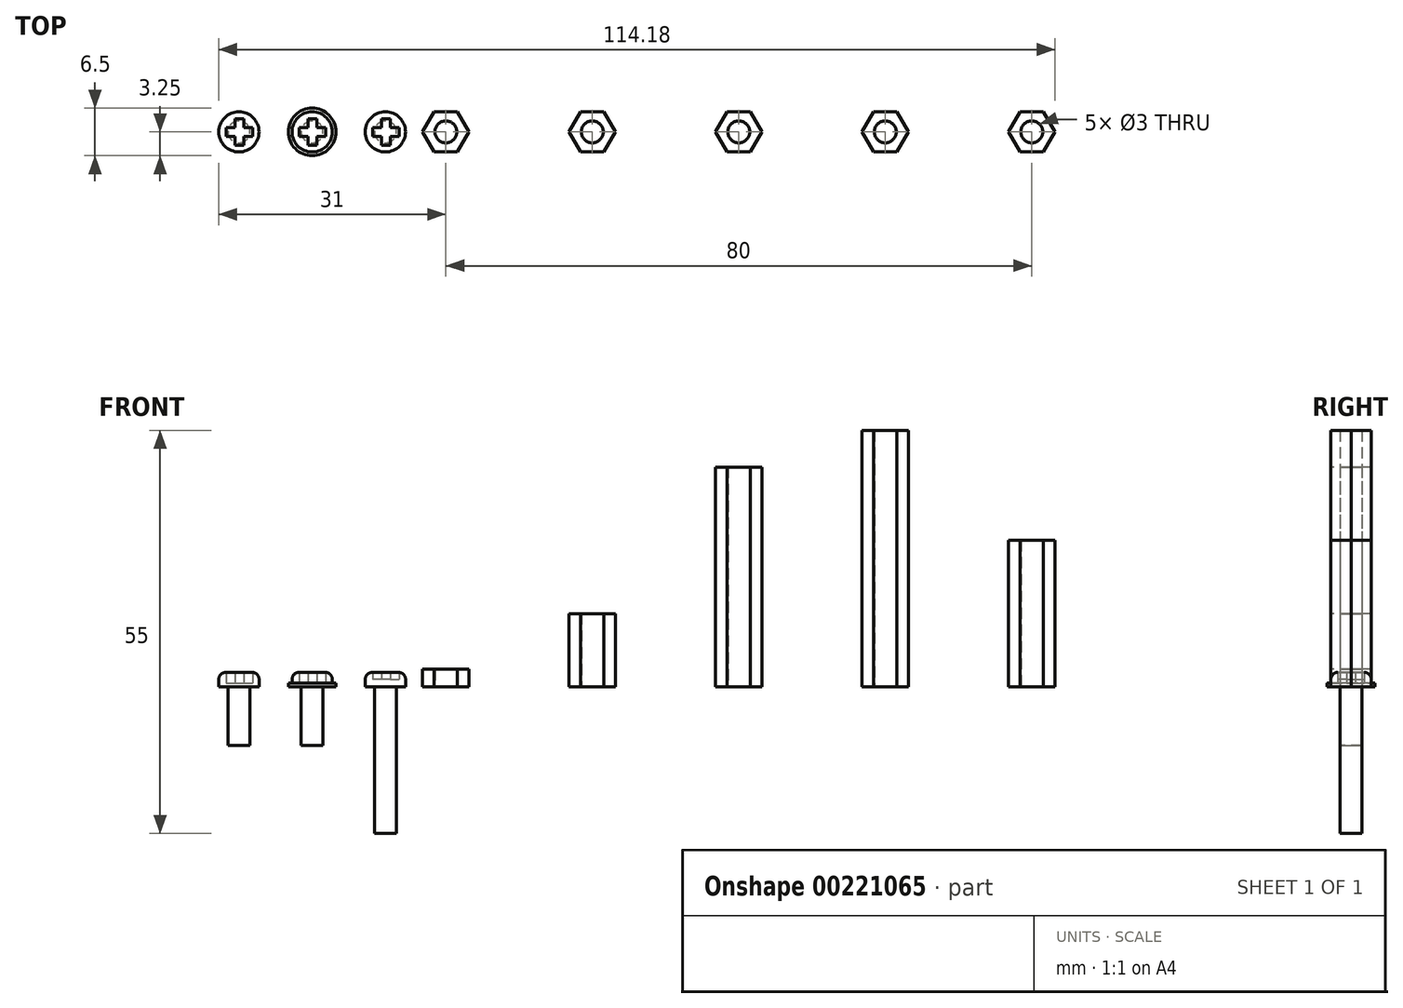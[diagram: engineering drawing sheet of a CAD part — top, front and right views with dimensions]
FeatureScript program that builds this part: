
annotation { "Feature Type Name" : "Feature", "Feature Type Description" : "" }
export const myFeature = defineFeature(function(context is Context, id is Id, definition is map)
    precondition{}
    {
        {
            var Q0;
            Q0=qCreatedBy(makeId("Top.planeOp"),FACE);
            var sketch = newSketch(context, id + "F0", { "sketchPlane" : qUnion([Q0])});
            skCircle(sketch, "E0", {"center": v(0, 0) * mm, "radius": 1.5 * mm});
            skCircle(sketch, "E1.cCircle", {"center": v(0, 0) * mm, "radius": 2.75 * mm, "construction": true});
            skLineSegment(sketch, "E1.0", {"start": v(3.18, 0) * mm, "end": v(1.59, -2.75) * mm});
            skLineSegment(sketch, "E1.1", {"start": v(1.59, -2.75) * mm, "end": v(-1.59, -2.75) * mm});
            skLineSegment(sketch, "E1.2", {"start": v(-1.59, -2.75) * mm, "end": v(-3.18, 0) * mm});
            skLineSegment(sketch, "E1.3", {"start": v(-3.18, 0) * mm, "end": v(-1.59, 2.75) * mm});
            skLineSegment(sketch, "E1.4", {"start": v(-1.59, 2.75) * mm, "end": v(1.59, 2.75) * mm});
            skLineSegment(sketch, "E1.5", {"start": v(1.59, 2.75) * mm, "end": v(3.18, 0) * mm});
            skPoint(sketch, "E1.0.midPoint", {"position": v(2.38, -1.37) * mm});
            skSolve(sketch);
        }
        {
            var Q0;
            Q0=makeQuery(id+"F0.imprint","IMPRINT",FACE,{"disambiguationData":[TD([[makeQuery(id+"F0.imprint","IMPRINT",EDGE,{"derivedFrom":sQuery(id+"F0.wireOp",EDGE,"E0")}),-1.0]])]});
            extrude(context, id + "F1", {"entities" : qUnion([Q0]), "depth" : 2.4 * mm});
        }
        {
            var Q0;
            Q0 = qSketchRegion(id + "F0", true);
            extrude(context, id + "F2", {"entities" : qUnion([Q0]), "depth" : 10 * mm});
        }
        {
            var Q0;
            Q0 = qSketchRegion(id + "F0", true);
            extrude(context, id + "F3", {"entities" : qUnion([Q0]), "depth" : 30 * mm});
        }
        {
            var Q0;
            Q0=qCreatedBy(makeId("Top.planeOp"),FACE);
            var sketch = newSketch(context, id + "F4", { "sketchPlane" : qUnion([Q0])});
            skCircle(sketch, "E2", {"center": v(-8.25, 0) * mm, "radius": 1.5 * mm});
            skCircle(sketch, "E3", {"center": v(-8.25, 0) * mm, "radius": 2.75 * mm});
            skLineSegment(sketch, "E4", {"start": v(-10, 0.6) * mm, "end": v(-10, -0.6) * mm});
            skLineSegment(sketch, "E5", {"start": v(-10, -0.6) * mm, "end": v(-8.8, -0.6) * mm});
            skLineSegment(sketch, "E6", {"start": v(-8.8, -0.6) * mm, "end": v(-8.8, -1.8) * mm});
            skLineSegment(sketch, "E7", {"start": v(-8.8, -1.8) * mm, "end": v(-7.6, -1.8) * mm});
            skLineSegment(sketch, "E8", {"start": v(-7.6, -1.8) * mm, "end": v(-7.6, -0.6) * mm});
            skLineSegment(sketch, "E9", {"start": v(-7.6, -0.6) * mm, "end": v(-6.4, -0.6) * mm});
            skLineSegment(sketch, "E10", {"start": v(-6.4, -0.6) * mm, "end": v(-6.4, 0.6) * mm});
            skLineSegment(sketch, "E11", {"start": v(-6.4, 0.6) * mm, "end": v(-7.6, 0.6) * mm});
            skLineSegment(sketch, "E12", {"start": v(-7.6, 0.6) * mm, "end": v(-7.6, 1.8) * mm});
            skLineSegment(sketch, "E13", {"start": v(-7.6, 1.8) * mm, "end": v(-8.8, 1.8) * mm});
            skLineSegment(sketch, "E14", {"start": v(-8.8, 1.8) * mm, "end": v(-8.8, 0.6) * mm});
            skLineSegment(sketch, "E15", {"start": v(-8.8, 0.6) * mm, "end": v(-10, 0.6) * mm});
            skPoint(sketch, "E16", {"position": v(-6.4, 0) * mm});
            skCircle(sketch, "E17", {"center": v(-8.25, 0) * mm, "radius": 3.25 * mm});
            skSolve(sketch);
        }
        {
            var Q0;
            Q0=makeQuery(id+"F4.imprint","IMPRINT",FACE,{"disambiguationData":[TD([[makeQuery(id+"F4.imprint","IMPRINT",EDGE,{"derivedFrom":sQuery(id+"F4.wireOp",EDGE,"E3")}),1.0]])]});
            var Q1;
            {var subQ0=sQuery(id+"F4.wireOp",EDGE,"E5");var subQ1=sQuery(id+"F4.wireOp",EDGE,"E2");var subQ2=makeQuery(id+"F4.imprint","INTERSECT",VERTEX,{"derivedFrom":[subQ1,subQ0]});Q1=makeQuery(id+"F4.imprint","IMPRINT",FACE,{"disambiguationData":[TD([[makeQuery(id+"F4.imprint","IMPRINT",EDGE,{"disambiguationData":[TD([[subQ2,-1.0]])],"derivedFrom":subQ1}),1.0]])]});}
            var Q2;
            {var subQ5=sQuery(id+"F4.wireOp",EDGE,"E4");Q2=makeQuery(id+"F4.imprint","IMPRINT",FACE,{"disambiguationData":[TD([[makeQuery(id+"F4.imprint","IMPRINT",EDGE,{"derivedFrom":subQ5}),1.0]])]});}
            var Q3;
            {var subQ5=sQuery(id+"F4.wireOp",EDGE,"E7");Q3=makeQuery(id+"F4.imprint","IMPRINT",FACE,{"disambiguationData":[TD([[makeQuery(id+"F4.imprint","IMPRINT",EDGE,{"derivedFrom":subQ5}),1.0]])]});}
            var Q4;
            {var subQ0=sQuery(id+"F4.wireOp",EDGE,"E8");var subQ1=sQuery(id+"F4.wireOp",EDGE,"E2");var subQ2=makeQuery(id+"F4.imprint","INTERSECT",VERTEX,{"derivedFrom":[subQ1,subQ0]});Q4=makeQuery(id+"F4.imprint","IMPRINT",FACE,{"disambiguationData":[TD([[makeQuery(id+"F4.imprint","IMPRINT",EDGE,{"disambiguationData":[TD([[subQ2,-1.0]])],"derivedFrom":subQ1}),1.0]])]});}
            var Q5;
            {var subQ5=sQuery(id+"F4.wireOp",EDGE,"E10");Q5=makeQuery(id+"F4.imprint","IMPRINT",FACE,{"disambiguationData":[TD([[makeQuery(id+"F4.imprint","IMPRINT",EDGE,{"derivedFrom":subQ5}),1.0]])]});}
            var Q6;
            {var subQ0=sQuery(id+"F4.wireOp",EDGE,"E12");var subQ1=sQuery(id+"F4.wireOp",EDGE,"E2");var subQ2=makeQuery(id+"F4.imprint","INTERSECT",VERTEX,{"derivedFrom":[subQ1,subQ0]});Q6=makeQuery(id+"F4.imprint","IMPRINT",FACE,{"disambiguationData":[TD([[makeQuery(id+"F4.imprint","IMPRINT",EDGE,{"disambiguationData":[TD([[subQ2,1.0]])],"derivedFrom":subQ1}),1.0]])]});}
            var Q7;
            {var subQ5=sQuery(id+"F4.wireOp",EDGE,"E13");Q7=makeQuery(id+"F4.imprint","IMPRINT",FACE,{"disambiguationData":[TD([[makeQuery(id+"F4.imprint","IMPRINT",EDGE,{"derivedFrom":subQ5}),1.0]])]});}
            var Q8;
            {var subQ0=sQuery(id+"F4.wireOp",EDGE,"E14");var subQ1=sQuery(id+"F4.wireOp",EDGE,"E2");var subQ2=makeQuery(id+"F4.imprint","INTERSECT",VERTEX,{"derivedFrom":[subQ1,subQ0]});Q8=makeQuery(id+"F4.imprint","IMPRINT",FACE,{"disambiguationData":[TD([[makeQuery(id+"F4.imprint","IMPRINT",EDGE,{"disambiguationData":[TD([[subQ2,-1.0]])],"derivedFrom":subQ1}),1.0]])]});}
            var Q9;
            {var subQ0=sQuery(id+"F4.wireOp",EDGE,"E12");var subQ3=sQuery(id+"F4.wireOp",EDGE,"E2");var subQ10=makeQuery(id+"F4.imprint","INTERSECT",VERTEX,{"derivedFrom":[subQ3,subQ0]});Q9=makeQuery(id+"F4.imprint","IMPRINT",FACE,{"disambiguationData":[TD([[makeQuery(id+"F4.imprint","IMPRINT",EDGE,{"disambiguationData":[TD([[subQ10,-1.0]])],"derivedFrom":subQ3}),1.0]])]});}
            extrude(context, id + "F5", {"entities" : qUnion([Q0, Q1, Q2, Q3, Q4, Q5, Q6, Q7, Q8, Q9]), "depth" : 2 * mm});
        }
        {
            var Q0;
            {var subQ5=sQuery(id+"F4.wireOp",EDGE,"E4");Q0=makeQuery(id+"F4.imprint","IMPRINT",FACE,{"disambiguationData":[TD([[makeQuery(id+"F4.imprint","IMPRINT",EDGE,{"derivedFrom":subQ5}),1.0]])]});}
            var Q1;
            {var subQ0=sQuery(id+"F4.wireOp",EDGE,"E12");var subQ3=sQuery(id+"F4.wireOp",EDGE,"E2");var subQ10=makeQuery(id+"F4.imprint","INTERSECT",VERTEX,{"derivedFrom":[subQ3,subQ0]});Q1=makeQuery(id+"F4.imprint","IMPRINT",FACE,{"disambiguationData":[TD([[makeQuery(id+"F4.imprint","IMPRINT",EDGE,{"disambiguationData":[TD([[subQ10,-1.0]])],"derivedFrom":subQ3}),1.0]])]});}
            var Q2;
            {var subQ5=sQuery(id+"F4.wireOp",EDGE,"E10");Q2=makeQuery(id+"F4.imprint","IMPRINT",FACE,{"disambiguationData":[TD([[makeQuery(id+"F4.imprint","IMPRINT",EDGE,{"derivedFrom":subQ5}),1.0]])]});}
            var Q3;
            {var subQ5=sQuery(id+"F4.wireOp",EDGE,"E7");Q3=makeQuery(id+"F4.imprint","IMPRINT",FACE,{"disambiguationData":[TD([[makeQuery(id+"F4.imprint","IMPRINT",EDGE,{"derivedFrom":subQ5}),1.0]])]});}
            var Q4;
            {var subQ5=sQuery(id+"F4.wireOp",EDGE,"E13");Q4=makeQuery(id+"F4.imprint","IMPRINT",FACE,{"disambiguationData":[TD([[makeQuery(id+"F4.imprint","IMPRINT",EDGE,{"derivedFrom":subQ5}),1.0]])]});}
            extrude(context, id + "F6", {"entities" : qUnion([Q0, Q1, Q2, Q3, Q4]), "operationType" : NewBodyOperationType.REMOVE, "depth" : 2 * mm});
        }
        {
            var Q0;
            Q0=makeQuery(id+"F4.imprint","IMPRINT",FACE,{"disambiguationData":[TD([[makeQuery(id+"F4.imprint","IMPRINT",EDGE,{"derivedFrom":sQuery(id+"F4.wireOp",EDGE,"E3")}),1.0]])]});
            var Q1;
            {var subQ0=sQuery(id+"F4.wireOp",EDGE,"E5");var subQ1=sQuery(id+"F4.wireOp",EDGE,"E2");var subQ2=makeQuery(id+"F4.imprint","INTERSECT",VERTEX,{"derivedFrom":[subQ1,subQ0]});Q1=makeQuery(id+"F4.imprint","IMPRINT",FACE,{"disambiguationData":[TD([[makeQuery(id+"F4.imprint","IMPRINT",EDGE,{"disambiguationData":[TD([[subQ2,-1.0]])],"derivedFrom":subQ1}),1.0]])]});}
            var Q2;
            {var subQ5=sQuery(id+"F4.wireOp",EDGE,"E7");Q2=makeQuery(id+"F4.imprint","IMPRINT",FACE,{"disambiguationData":[TD([[makeQuery(id+"F4.imprint","IMPRINT",EDGE,{"derivedFrom":subQ5}),1.0]])]});}
            var Q3;
            {var subQ0=sQuery(id+"F4.wireOp",EDGE,"E8");var subQ1=sQuery(id+"F4.wireOp",EDGE,"E2");var subQ2=makeQuery(id+"F4.imprint","INTERSECT",VERTEX,{"derivedFrom":[subQ1,subQ0]});Q3=makeQuery(id+"F4.imprint","IMPRINT",FACE,{"disambiguationData":[TD([[makeQuery(id+"F4.imprint","IMPRINT",EDGE,{"disambiguationData":[TD([[subQ2,-1.0]])],"derivedFrom":subQ1}),1.0]])]});}
            var Q4;
            {var subQ5=sQuery(id+"F4.wireOp",EDGE,"E10");Q4=makeQuery(id+"F4.imprint","IMPRINT",FACE,{"disambiguationData":[TD([[makeQuery(id+"F4.imprint","IMPRINT",EDGE,{"derivedFrom":subQ5}),1.0]])]});}
            var Q5;
            {var subQ0=sQuery(id+"F4.wireOp",EDGE,"E12");var subQ3=sQuery(id+"F4.wireOp",EDGE,"E2");var subQ10=makeQuery(id+"F4.imprint","INTERSECT",VERTEX,{"derivedFrom":[subQ3,subQ0]});Q5=makeQuery(id+"F4.imprint","IMPRINT",FACE,{"disambiguationData":[TD([[makeQuery(id+"F4.imprint","IMPRINT",EDGE,{"disambiguationData":[TD([[subQ10,-1.0]])],"derivedFrom":subQ3}),1.0]])]});}
            var Q6;
            {var subQ5=sQuery(id+"F4.wireOp",EDGE,"E13");Q6=makeQuery(id+"F4.imprint","IMPRINT",FACE,{"disambiguationData":[TD([[makeQuery(id+"F4.imprint","IMPRINT",EDGE,{"derivedFrom":subQ5}),1.0]])]});}
            var Q7;
            {var subQ0=sQuery(id+"F4.wireOp",EDGE,"E14");var subQ1=sQuery(id+"F4.wireOp",EDGE,"E2");var subQ2=makeQuery(id+"F4.imprint","INTERSECT",VERTEX,{"derivedFrom":[subQ1,subQ0]});Q7=makeQuery(id+"F4.imprint","IMPRINT",FACE,{"disambiguationData":[TD([[makeQuery(id+"F4.imprint","IMPRINT",EDGE,{"disambiguationData":[TD([[subQ2,-1.0]])],"derivedFrom":subQ1}),1.0]])]});}
            var Q8;
            {var subQ0=sQuery(id+"F4.wireOp",EDGE,"E12");var subQ1=sQuery(id+"F4.wireOp",EDGE,"E2");var subQ2=makeQuery(id+"F4.imprint","INTERSECT",VERTEX,{"derivedFrom":[subQ1,subQ0]});Q8=makeQuery(id+"F4.imprint","IMPRINT",FACE,{"disambiguationData":[TD([[makeQuery(id+"F4.imprint","IMPRINT",EDGE,{"disambiguationData":[TD([[subQ2,1.0]])],"derivedFrom":subQ1}),1.0]])]});}
            var Q9;
            {var subQ5=sQuery(id+"F4.wireOp",EDGE,"E4");Q9=makeQuery(id+"F4.imprint","IMPRINT",FACE,{"disambiguationData":[TD([[makeQuery(id+"F4.imprint","IMPRINT",EDGE,{"derivedFrom":subQ5}),1.0]])]});}
            extrude(context, id + "F7", {"entities" : qUnion([Q0, Q1, Q2, Q3, Q4, Q5, Q6, Q7, Q8, Q9]), "operationType" : NewBodyOperationType.ADD, "depth" : 0.5 * mm});
        }
        {
            var Q0;
            {var subQ0=sQuery(id+"F4.wireOp",EDGE,"E5");var subQ1=sQuery(id+"F4.wireOp",EDGE,"E2");var subQ2=makeQuery(id+"F4.imprint","INTERSECT",VERTEX,{"derivedFrom":[subQ1,subQ0]});Q0=makeQuery(id+"F4.imprint","IMPRINT",FACE,{"disambiguationData":[TD([[makeQuery(id+"F4.imprint","IMPRINT",EDGE,{"disambiguationData":[TD([[subQ2,-1.0]])],"derivedFrom":subQ1}),1.0]])]});}
            var Q1;
            {var subQ0=sQuery(id+"F4.wireOp",EDGE,"E12");var subQ3=sQuery(id+"F4.wireOp",EDGE,"E2");var subQ10=makeQuery(id+"F4.imprint","INTERSECT",VERTEX,{"derivedFrom":[subQ3,subQ0]});Q1=makeQuery(id+"F4.imprint","IMPRINT",FACE,{"disambiguationData":[TD([[makeQuery(id+"F4.imprint","IMPRINT",EDGE,{"disambiguationData":[TD([[subQ10,-1.0]])],"derivedFrom":subQ3}),1.0]])]});}
            var Q2;
            {var subQ0=sQuery(id+"F4.wireOp",EDGE,"E8");var subQ1=sQuery(id+"F4.wireOp",EDGE,"E2");var subQ2=makeQuery(id+"F4.imprint","INTERSECT",VERTEX,{"derivedFrom":[subQ1,subQ0]});Q2=makeQuery(id+"F4.imprint","IMPRINT",FACE,{"disambiguationData":[TD([[makeQuery(id+"F4.imprint","IMPRINT",EDGE,{"disambiguationData":[TD([[subQ2,-1.0]])],"derivedFrom":subQ1}),1.0]])]});}
            var Q3;
            {var subQ0=sQuery(id+"F4.wireOp",EDGE,"E14");var subQ1=sQuery(id+"F4.wireOp",EDGE,"E2");var subQ2=makeQuery(id+"F4.imprint","INTERSECT",VERTEX,{"derivedFrom":[subQ1,subQ0]});Q3=makeQuery(id+"F4.imprint","IMPRINT",FACE,{"disambiguationData":[TD([[makeQuery(id+"F4.imprint","IMPRINT",EDGE,{"disambiguationData":[TD([[subQ2,-1.0]])],"derivedFrom":subQ1}),1.0]])]});}
            var Q4;
            {var subQ0=sQuery(id+"F4.wireOp",EDGE,"E12");var subQ1=sQuery(id+"F4.wireOp",EDGE,"E2");var subQ2=makeQuery(id+"F4.imprint","INTERSECT",VERTEX,{"derivedFrom":[subQ1,subQ0]});Q4=makeQuery(id+"F4.imprint","IMPRINT",FACE,{"disambiguationData":[TD([[makeQuery(id+"F4.imprint","IMPRINT",EDGE,{"disambiguationData":[TD([[subQ2,1.0]])],"derivedFrom":subQ1}),1.0]])]});}
            extrude(context, id + "F8", {"entities" : qUnion([Q0, Q1, Q2, Q3, Q4]), "operationType" : NewBodyOperationType.ADD, "oppositeDirection" : true, "depth" : 8 * mm});
        }
        {
            var Q0;
            Q0=makeQuery(id+"F2.opExtrude","SWEPT_BODY",BODY,{"disambiguationData":[OSD([sQuery(id+"F0.wireOp",EDGE,"E0"),sQuery(id+"F0.wireOp",EDGE,"E1.0"),sQuery(id+"F0.wireOp",EDGE,"E1.1"),sQuery(id+"F0.wireOp",EDGE,"E1.2"),sQuery(id+"F0.wireOp",EDGE,"E1.3"),sQuery(id+"F0.wireOp",EDGE,"E1.4"),sQuery(id+"F0.wireOp",EDGE,"E1.5")])]});
            transform(context, id + "F9", {"entities" : qUnion([Q0]), "transformType" : TransformType.TRANSLATION_3D, "dx" : 20 * mm, "dy" : 0 * mm, "dz" : 0 * mm, "makeCopy" : false});
        }
        {
            var Q0;
            Q0=makeQuery(id+"F3.opExtrude","SWEPT_BODY",BODY,{"disambiguationData":[OSD([sQuery(id+"F0.wireOp",EDGE,"E0"),sQuery(id+"F0.wireOp",EDGE,"E1.0"),sQuery(id+"F0.wireOp",EDGE,"E1.1"),sQuery(id+"F0.wireOp",EDGE,"E1.2"),sQuery(id+"F0.wireOp",EDGE,"E1.3"),sQuery(id+"F0.wireOp",EDGE,"E1.4"),sQuery(id+"F0.wireOp",EDGE,"E1.5")])]});
            transform(context, id + "F10", {"entities" : qUnion([Q0]), "transformType" : TransformType.TRANSLATION_3D, "dx" : 40 * mm, "dy" : 0 * mm, "dz" : 0 * mm, "makeCopy" : false});
        }
        {
            var Q0;
            Q0=makeQuery(id+"F5.opExtrude","SWEPT_BODY",BODY,{"disambiguationData":[OSD([sQuery(id+"F4.wireOp",EDGE,"E3")])]});
            transform(context, id + "F11", {"entities" : qUnion([Q0]), "transformType" : TransformType.TRANSLATION_3D, "dx" : (-20) * mm, "dy" : 0 * mm, "dz" : 0 * mm, "makeCopy" : true});
        }
        {
            var Q0;
            Q0=makeQuery(id+"F4.imprint","IMPRINT",FACE,{"disambiguationData":[TD([[makeQuery(id+"F4.imprint","IMPRINT",EDGE,{"derivedFrom":sQuery(id+"F4.wireOp",EDGE,"E3")}),-1.0]])]});
            extrude(context, id + "F12", {"entities" : qUnion([Q0]), "operationType" : NewBodyOperationType.ADD, "depth" : 0.5 * mm});
        }
        {
            var Q0;
            Q0=makeQuery(id+"F11.opPattern","COPY",EDGE,{"derivedFrom":makeQuery(id+"F5.opExtrude","CAP_EDGE",EDGE,{"disambiguationData":[OSD([sQuery(id+"F4.wireOp",EDGE,"E3")])],"isStart":false}),"instanceName":"1"});
            var Q1;
            Q1=makeQuery(id+"F5.opExtrude","CAP_EDGE",EDGE,{"disambiguationData":[OSD([sQuery(id+"F4.wireOp",EDGE,"E3")])],"isStart":false});
            fillet(context, id + "F13", {"entities" : qUnion([Q0, Q1]), "radius" : 1 * mm, "tangentPropagation" : true, "allowEdgeOverflow" : false});
        }
        {
            var Q0;
            Q0 = qSketchRegion(id + "F0", true);
            extrude(context, id + "F14", {"entities" : qUnion([Q0]), "depth" : 35 * mm});
        }
        {
            var Q0;
            Q0=makeQuery(id+"F14.opExtrude","SWEPT_BODY",BODY,{"disambiguationData":[OSD([sQuery(id+"F0.wireOp",EDGE,"E0"),sQuery(id+"F0.wireOp",EDGE,"E1.0"),sQuery(id+"F0.wireOp",EDGE,"E1.1"),sQuery(id+"F0.wireOp",EDGE,"E1.2"),sQuery(id+"F0.wireOp",EDGE,"E1.3"),sQuery(id+"F0.wireOp",EDGE,"E1.4"),sQuery(id+"F0.wireOp",EDGE,"E1.5")])]});
            transform(context, id + "F15", {"entities" : qUnion([Q0]), "transformType" : TransformType.TRANSLATION_3D, "dx" : 60 * mm, "dy" : 0 * mm, "dz" : 0 * mm, "makeCopy" : false});
        }
        {
            var Q0;
            Q0 = qSketchRegion(id + "F0", true);
            extrude(context, id + "F16", {"entities" : qUnion([Q0]), "depth" : 20 * mm});
        }
        {
            var Q0;
            Q0=makeQuery(id+"F16.opExtrude","SWEPT_BODY",BODY,{"disambiguationData":[OSD([sQuery(id+"F0.wireOp",EDGE,"E0"),sQuery(id+"F0.wireOp",EDGE,"E1.0"),sQuery(id+"F0.wireOp",EDGE,"E1.1"),sQuery(id+"F0.wireOp",EDGE,"E1.2"),sQuery(id+"F0.wireOp",EDGE,"E1.3"),sQuery(id+"F0.wireOp",EDGE,"E1.4"),sQuery(id+"F0.wireOp",EDGE,"E1.5")])]});
            transform(context, id + "F17", {"entities" : qUnion([Q0]), "transformType" : TransformType.TRANSLATION_3D, "dx" : 80 * mm, "dy" : 0 * mm, "dz" : 0 * mm, "makeCopy" : false});
        }
        {
            var Q0;
            Q0=makeQuery(id+"F5.opExtrude","SWEPT_BODY",BODY,{"disambiguationData":[OSD([sQuery(id+"F4.wireOp",EDGE,"E3")])]});
            transform(context, id + "F18", {"entities" : qUnion([Q0]), "transformType" : TransformType.TRANSLATION_3D, "dx" : -10 * mm, "dy" : 0 * mm, "dz" : 0 * mm, "makeCopy" : false});
        }
        {
            var Q0;
            Q0=makeQuery(id+"F4.imprint","IMPRINT",FACE,{"disambiguationData":[TD([[makeQuery(id+"F4.imprint","IMPRINT",EDGE,{"derivedFrom":sQuery(id+"F4.wireOp",EDGE,"E3")}),1.0]])]});
            var Q1;
            {var subQ5=sQuery(id+"F4.wireOp",EDGE,"E10");Q1=makeQuery(id+"F4.imprint","IMPRINT",FACE,{"disambiguationData":[TD([[makeQuery(id+"F4.imprint","IMPRINT",EDGE,{"derivedFrom":subQ5}),1.0]])]});}
            var Q2;
            {var subQ0=sQuery(id+"F4.wireOp",EDGE,"E8");var subQ1=sQuery(id+"F4.wireOp",EDGE,"E2");var subQ2=makeQuery(id+"F4.imprint","INTERSECT",VERTEX,{"derivedFrom":[subQ1,subQ0]});Q2=makeQuery(id+"F4.imprint","IMPRINT",FACE,{"disambiguationData":[TD([[makeQuery(id+"F4.imprint","IMPRINT",EDGE,{"disambiguationData":[TD([[subQ2,-1.0]])],"derivedFrom":subQ1}),1.0]])]});}
            var Q3;
            {var subQ0=sQuery(id+"F4.wireOp",EDGE,"E5");var subQ1=sQuery(id+"F4.wireOp",EDGE,"E2");var subQ2=makeQuery(id+"F4.imprint","INTERSECT",VERTEX,{"derivedFrom":[subQ1,subQ0]});Q3=makeQuery(id+"F4.imprint","IMPRINT",FACE,{"disambiguationData":[TD([[makeQuery(id+"F4.imprint","IMPRINT",EDGE,{"disambiguationData":[TD([[subQ2,-1.0]])],"derivedFrom":subQ1}),1.0]])]});}
            var Q4;
            {var subQ5=sQuery(id+"F4.wireOp",EDGE,"E7");Q4=makeQuery(id+"F4.imprint","IMPRINT",FACE,{"disambiguationData":[TD([[makeQuery(id+"F4.imprint","IMPRINT",EDGE,{"derivedFrom":subQ5}),1.0]])]});}
            var Q5;
            {var subQ5=sQuery(id+"F4.wireOp",EDGE,"E4");Q5=makeQuery(id+"F4.imprint","IMPRINT",FACE,{"disambiguationData":[TD([[makeQuery(id+"F4.imprint","IMPRINT",EDGE,{"derivedFrom":subQ5}),1.0]])]});}
            var Q6;
            {var subQ5=sQuery(id+"F4.wireOp",EDGE,"E13");Q6=makeQuery(id+"F4.imprint","IMPRINT",FACE,{"disambiguationData":[TD([[makeQuery(id+"F4.imprint","IMPRINT",EDGE,{"derivedFrom":subQ5}),1.0]])]});}
            var Q7;
            {var subQ0=sQuery(id+"F4.wireOp",EDGE,"E12");var subQ1=sQuery(id+"F4.wireOp",EDGE,"E2");var subQ2=makeQuery(id+"F4.imprint","INTERSECT",VERTEX,{"derivedFrom":[subQ1,subQ0]});Q7=makeQuery(id+"F4.imprint","IMPRINT",FACE,{"disambiguationData":[TD([[makeQuery(id+"F4.imprint","IMPRINT",EDGE,{"disambiguationData":[TD([[subQ2,1.0]])],"derivedFrom":subQ1}),1.0]])]});}
            var Q8;
            {var subQ0=sQuery(id+"F4.wireOp",EDGE,"E14");var subQ1=sQuery(id+"F4.wireOp",EDGE,"E2");var subQ2=makeQuery(id+"F4.imprint","INTERSECT",VERTEX,{"derivedFrom":[subQ1,subQ0]});Q8=makeQuery(id+"F4.imprint","IMPRINT",FACE,{"disambiguationData":[TD([[makeQuery(id+"F4.imprint","IMPRINT",EDGE,{"disambiguationData":[TD([[subQ2,-1.0]])],"derivedFrom":subQ1}),1.0]])]});}
            var Q9;
            {var subQ0=sQuery(id+"F4.wireOp",EDGE,"E12");var subQ3=sQuery(id+"F4.wireOp",EDGE,"E2");var subQ10=makeQuery(id+"F4.imprint","INTERSECT",VERTEX,{"derivedFrom":[subQ3,subQ0]});Q9=makeQuery(id+"F4.imprint","IMPRINT",FACE,{"disambiguationData":[TD([[makeQuery(id+"F4.imprint","IMPRINT",EDGE,{"disambiguationData":[TD([[subQ10,-1.0]])],"derivedFrom":subQ3}),1.0]])]});}
            extrude(context, id + "F19", {"entities" : qUnion([Q0, Q1, Q2, Q3, Q4, Q5, Q6, Q7, Q8, Q9]), "depth" : 2 * mm});
        }
        {
            var Q0;
            {var subQ0=sQuery(id+"F4.wireOp",EDGE,"E12");var subQ3=sQuery(id+"F4.wireOp",EDGE,"E2");var subQ10=makeQuery(id+"F4.imprint","INTERSECT",VERTEX,{"derivedFrom":[subQ3,subQ0]});Q0=makeQuery(id+"F4.imprint","IMPRINT",FACE,{"disambiguationData":[TD([[makeQuery(id+"F4.imprint","IMPRINT",EDGE,{"disambiguationData":[TD([[subQ10,-1.0]])],"derivedFrom":subQ3}),1.0]])]});}
            var Q1;
            {var subQ5=sQuery(id+"F4.wireOp",EDGE,"E7");Q1=makeQuery(id+"F4.imprint","IMPRINT",FACE,{"disambiguationData":[TD([[makeQuery(id+"F4.imprint","IMPRINT",EDGE,{"derivedFrom":subQ5}),1.0]])]});}
            var Q2;
            {var subQ5=sQuery(id+"F4.wireOp",EDGE,"E4");Q2=makeQuery(id+"F4.imprint","IMPRINT",FACE,{"disambiguationData":[TD([[makeQuery(id+"F4.imprint","IMPRINT",EDGE,{"derivedFrom":subQ5}),1.0]])]});}
            var Q3;
            {var subQ5=sQuery(id+"F4.wireOp",EDGE,"E13");Q3=makeQuery(id+"F4.imprint","IMPRINT",FACE,{"disambiguationData":[TD([[makeQuery(id+"F4.imprint","IMPRINT",EDGE,{"derivedFrom":subQ5}),1.0]])]});}
            var Q4;
            {var subQ5=sQuery(id+"F4.wireOp",EDGE,"E10");Q4=makeQuery(id+"F4.imprint","IMPRINT",FACE,{"disambiguationData":[TD([[makeQuery(id+"F4.imprint","IMPRINT",EDGE,{"derivedFrom":subQ5}),1.0]])]});}
            extrude(context, id + "F20", {"entities" : qUnion([Q0, Q1, Q2, Q3, Q4]), "operationType" : NewBodyOperationType.REMOVE, "depth" : 2 * mm});
        }
        {
            var Q0;
            Q0=makeQuery(id+"F4.imprint","IMPRINT",FACE,{"disambiguationData":[TD([[makeQuery(id+"F4.imprint","IMPRINT",EDGE,{"derivedFrom":sQuery(id+"F4.wireOp",EDGE,"E3")}),1.0]])]});
            var Q1;
            {var subQ5=sQuery(id+"F4.wireOp",EDGE,"E7");Q1=makeQuery(id+"F4.imprint","IMPRINT",FACE,{"disambiguationData":[TD([[makeQuery(id+"F4.imprint","IMPRINT",EDGE,{"derivedFrom":subQ5}),1.0]])]});}
            var Q2;
            {var subQ5=sQuery(id+"F4.wireOp",EDGE,"E10");Q2=makeQuery(id+"F4.imprint","IMPRINT",FACE,{"disambiguationData":[TD([[makeQuery(id+"F4.imprint","IMPRINT",EDGE,{"derivedFrom":subQ5}),1.0]])]});}
            var Q3;
            {var subQ5=sQuery(id+"F4.wireOp",EDGE,"E4");Q3=makeQuery(id+"F4.imprint","IMPRINT",FACE,{"disambiguationData":[TD([[makeQuery(id+"F4.imprint","IMPRINT",EDGE,{"derivedFrom":subQ5}),1.0]])]});}
            var Q4;
            {var subQ5=sQuery(id+"F4.wireOp",EDGE,"E13");Q4=makeQuery(id+"F4.imprint","IMPRINT",FACE,{"disambiguationData":[TD([[makeQuery(id+"F4.imprint","IMPRINT",EDGE,{"derivedFrom":subQ5}),1.0]])]});}
            var Q5;
            {var subQ0=sQuery(id+"F4.wireOp",EDGE,"E12");var subQ3=sQuery(id+"F4.wireOp",EDGE,"E2");var subQ10=makeQuery(id+"F4.imprint","INTERSECT",VERTEX,{"derivedFrom":[subQ3,subQ0]});Q5=makeQuery(id+"F4.imprint","IMPRINT",FACE,{"disambiguationData":[TD([[makeQuery(id+"F4.imprint","IMPRINT",EDGE,{"disambiguationData":[TD([[subQ10,-1.0]])],"derivedFrom":subQ3}),1.0]])]});}
            extrude(context, id + "F21", {"entities" : qUnion([Q0, Q1, Q2, Q3, Q4, Q5]), "operationType" : NewBodyOperationType.ADD, "depth" : 1 * mm});
        }
        {
            var Q0;
            {var subQ0=sQuery(id+"F4.wireOp",EDGE,"E5");var subQ1=sQuery(id+"F4.wireOp",EDGE,"E2");var subQ2=makeQuery(id+"F4.imprint","INTERSECT",VERTEX,{"derivedFrom":[subQ1,subQ0]});Q0=makeQuery(id+"F4.imprint","IMPRINT",FACE,{"disambiguationData":[TD([[makeQuery(id+"F4.imprint","IMPRINT",EDGE,{"disambiguationData":[TD([[subQ2,-1.0]])],"derivedFrom":subQ1}),1.0]])]});}
            var Q1;
            {var subQ0=sQuery(id+"F4.wireOp",EDGE,"E12");var subQ3=sQuery(id+"F4.wireOp",EDGE,"E2");var subQ10=makeQuery(id+"F4.imprint","INTERSECT",VERTEX,{"derivedFrom":[subQ3,subQ0]});Q1=makeQuery(id+"F4.imprint","IMPRINT",FACE,{"disambiguationData":[TD([[makeQuery(id+"F4.imprint","IMPRINT",EDGE,{"disambiguationData":[TD([[subQ10,-1.0]])],"derivedFrom":subQ3}),1.0]])]});}
            var Q2;
            {var subQ0=sQuery(id+"F4.wireOp",EDGE,"E8");var subQ1=sQuery(id+"F4.wireOp",EDGE,"E2");var subQ2=makeQuery(id+"F4.imprint","INTERSECT",VERTEX,{"derivedFrom":[subQ1,subQ0]});Q2=makeQuery(id+"F4.imprint","IMPRINT",FACE,{"disambiguationData":[TD([[makeQuery(id+"F4.imprint","IMPRINT",EDGE,{"disambiguationData":[TD([[subQ2,-1.0]])],"derivedFrom":subQ1}),1.0]])]});}
            var Q3;
            {var subQ0=sQuery(id+"F4.wireOp",EDGE,"E12");var subQ1=sQuery(id+"F4.wireOp",EDGE,"E2");var subQ2=makeQuery(id+"F4.imprint","INTERSECT",VERTEX,{"derivedFrom":[subQ1,subQ0]});Q3=makeQuery(id+"F4.imprint","IMPRINT",FACE,{"disambiguationData":[TD([[makeQuery(id+"F4.imprint","IMPRINT",EDGE,{"disambiguationData":[TD([[subQ2,1.0]])],"derivedFrom":subQ1}),1.0]])]});}
            var Q4;
            {var subQ0=sQuery(id+"F4.wireOp",EDGE,"E14");var subQ1=sQuery(id+"F4.wireOp",EDGE,"E2");var subQ2=makeQuery(id+"F4.imprint","INTERSECT",VERTEX,{"derivedFrom":[subQ1,subQ0]});Q4=makeQuery(id+"F4.imprint","IMPRINT",FACE,{"disambiguationData":[TD([[makeQuery(id+"F4.imprint","IMPRINT",EDGE,{"disambiguationData":[TD([[subQ2,-1.0]])],"derivedFrom":subQ1}),1.0]])]});}
            extrude(context, id + "F22", {"entities" : qUnion([Q0, Q1, Q2, Q3, Q4]), "operationType" : NewBodyOperationType.ADD, "oppositeDirection" : true, "depth" : 20 * mm});
        }
        {
            var Q0;
            Q0=makeQuery(id+"F19.opExtrude","CAP_EDGE",EDGE,{"disambiguationData":[OSD([sQuery(id+"F4.wireOp",EDGE,"E3")])],"isStart":false});
            fillet(context, id + "F23", {"entities" : qUnion([Q0]), "radius" : 1 * mm, "tangentPropagation" : true, "allowEdgeOverflow" : false});
        }
    });
